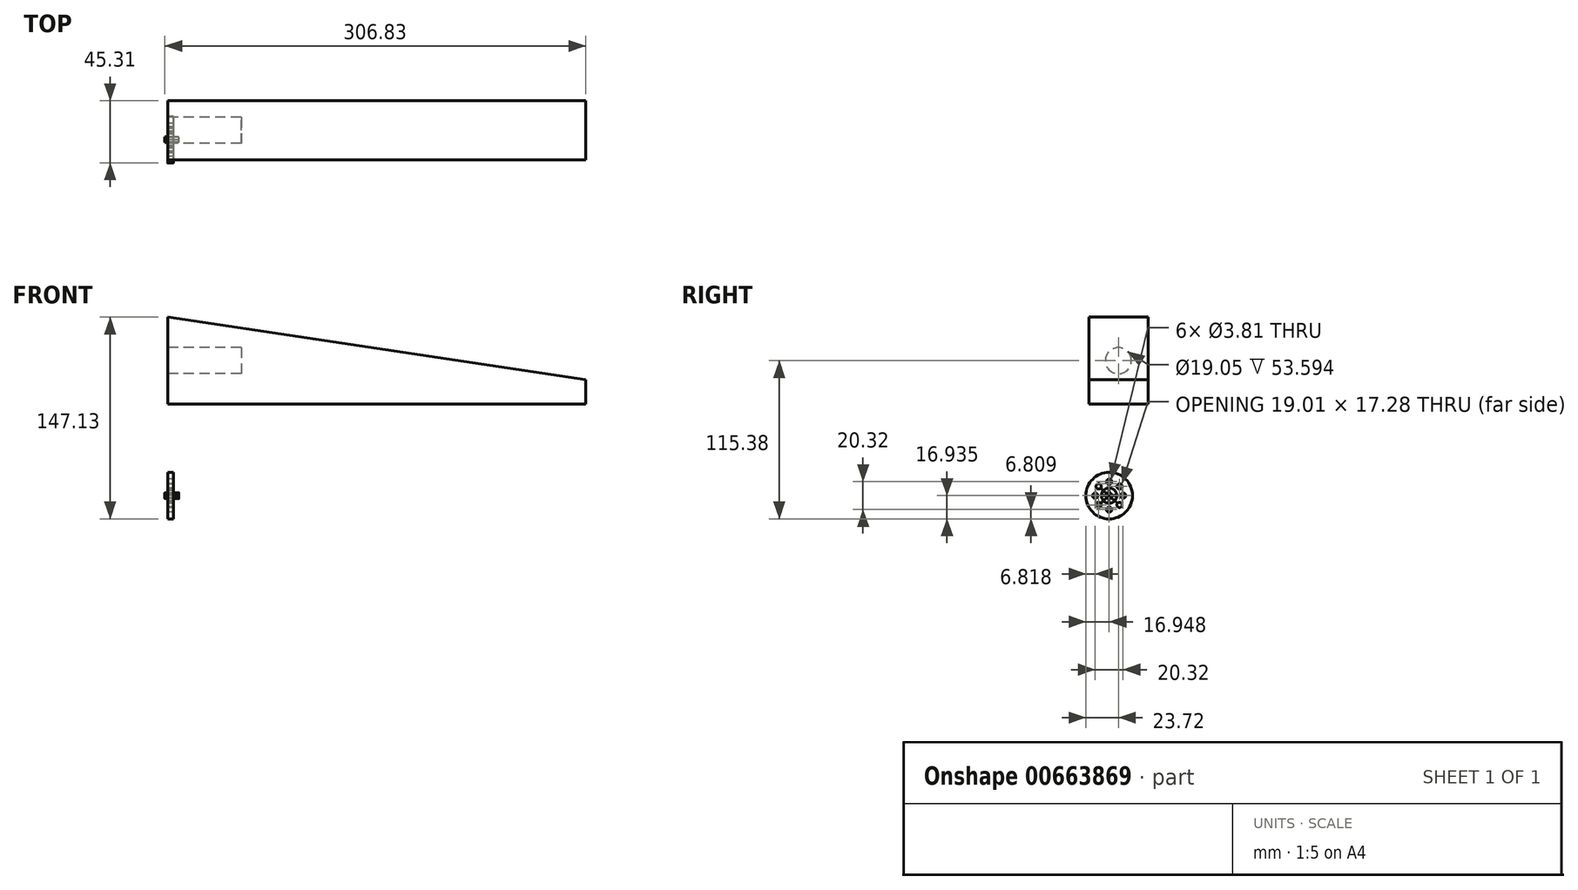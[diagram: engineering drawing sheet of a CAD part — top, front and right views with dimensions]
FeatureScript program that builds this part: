
annotation { "Feature Type Name" : "Feature", "Feature Type Description" : "" }
export const myFeature = defineFeature(function(context is Context, id is Id, definition is map)
    precondition{}
    {
        {
            var Q0;
            Q0=qCreatedBy(makeId("Front.planeOp"),FACE);
            var sketch = newSketch(context, id + "F0", { "sketchPlane" : qUnion([Q0])});
            skLineSegment(sketch, "E0", {"start": v(0, 0) * mm, "end": v(0, 63.5) * mm});
            skLineSegment(sketch, "E1", {"start": v(0, 0) * mm, "end": v(304.8, 0) * mm});
            skLineSegment(sketch, "E2", {"start": v(304.8, 0) * mm, "end": v(304.8, 17.78) * mm});
            skLineSegment(sketch, "E3", {"start": v(304.8, 17.78) * mm, "end": v(0, 63.5) * mm});
            skSolve(sketch);
        }
        {
            var Q0;
            Q0=makeQuery(id+"F0.imprint","IMPRINT",FACE,{"disambiguationData":[TD([[makeQuery(id+"F0.imprint","IMPRINT",EDGE,{"derivedFrom":sQuery(id+"F0.wireOp",EDGE,"E0")}),-1.0]])]});
            extrude(context, id + "F1", {"entities" : qUnion([Q0]), "oppositeDirection" : true, "depth" : 43.18 * mm, "offsetDistance" : 25.4 * mm});
        }
        {
            var Q0;
            Q0=makeQuery(id+"F1.opExtrude","SWEPT_FACE",FACE,{"disambiguationData":[OSD([sQuery(id+"F0.wireOp",EDGE,"E0")])]});
            var sketch = newSketch(context, id + "F2", { "sketchPlane" : qUnion([Q0])});
            skLineSegment(sketch, "E4", {"start": v(0, 0) * mm, "end": v(0, 31.75) * mm});
            skLineSegment(sketch, "E5", {"start": v(0, 31.75) * mm, "end": v(-21.59, 31.75) * mm});
            skCircle(sketch, "E6", {"center": v(-21.59, 31.75) * mm, "radius": 9.53 * mm});
            skSolve(sketch);
        }
        {
            var Q0;
            Q0=makeQuery(id+"F2.imprint","IMPRINT",FACE,{"disambiguationData":[TD([[makeQuery(id+"F2.imprint","IMPRINT",EDGE,{"derivedFrom":sQuery(id+"F2.wireOp",EDGE,"E6")}),1.0]])]});
            extrude(context, id + "F3", {"entities" : qUnion([Q0]), "operationType" : NewBodyOperationType.REMOVE, "oppositeDirection" : true, "depth" : 53.6 * mm, "offsetDistance" : 25.4 * mm});
        }
        {
            var Q0;
            Q0=qCreatedBy(makeId("Right.planeOp"),FACE);
            var sketch = newSketch(context, id + "F4", { "sketchPlane" : qUnion([Q0])});
            skCircle(sketch, "E7", {"center": v(14.85, -66.66) * mm, "radius": 16.97 * mm});
            skCircle(sketch, "E8", {"center": v(14.85, -66.66) * mm, "radius": 5.59 * mm});
            skCircle(sketch, "E9", {"center": v(14.85, -66.66) * mm, "radius": 2.16 * mm});
            skLineSegment(sketch, "E10", {"start": v(14.85, -66.66) * mm, "end": v(14.85, -76.82) * mm});
            skCircle(sketch, "E11", {"center": v(14.85, -76.82) * mm, "radius": 1.9 * mm});
            skLineSegment(sketch, "E12", {"start": v(14.85, -66.66) * mm, "end": v(14.85, -56.5) * mm});
            skCircle(sketch, "E13", {"center": v(14.85, -56.5) * mm, "radius": 1.9 * mm});
            skLineSegment(sketch, "E14", {"start": v(14.85, -66.66) * mm, "end": v(25, -66.66) * mm});
            skCircle(sketch, "E15", {"center": v(25, -66.66) * mm, "radius": 1.9 * mm});
            skLineSegment(sketch, "E16", {"start": v(14.85, -66.66) * mm, "end": v(4.69, -66.66) * mm});
            skCircle(sketch, "E17", {"center": v(4.69, -66.66) * mm, "radius": 1.9 * mm});
            skLineSegment(sketch, "E18", {"start": v(14.85, -66.66) * mm, "end": v(7.22, -59.95) * mm});
            skLineSegment(sketch, "E19", {"start": v(7.22, -59.95) * mm, "end": v(22.42, -73.44) * mm});
            skLineSegment(sketch, "E20", {"start": v(22.42, -73.44) * mm, "end": v(14.85, -66.66) * mm});
            skLineSegment(sketch, "E21", {"start": v(14.85, -66.66) * mm, "end": v(7.22, -73.44) * mm});
            skLineSegment(sketch, "E22", {"start": v(7.22, -73.44) * mm, "end": v(22.42, -59.95) * mm});
            skCircle(sketch, "E23", {"center": v(22.42, -59.95) * mm, "radius": 1.9 * mm});
            skCircle(sketch, "E24", {"center": v(22.42, -73.44) * mm, "radius": 1.9 * mm});
            skCircle(sketch, "E25", {"center": v(7.22, -73.44) * mm, "radius": 1.9 * mm});
            skCircle(sketch, "E26", {"center": v(7.22, -59.95) * mm, "radius": 1.9 * mm});
            skSolve(sketch);
        }
        {
            var Q0;
            {var subQ0=sQuery(id+"F4.wireOp",EDGE,"E10");var subQ1=sQuery(id+"F4.wireOp",EDGE,"E9");var subQ2=makeQuery(id+"F4.imprint","INTERSECT",VERTEX,{"derivedFrom":[subQ1,subQ0]});Q0=makeQuery(id+"F4.imprint","IMPRINT",FACE,{"disambiguationData":[TD([[makeQuery(id+"F4.imprint","IMPRINT",EDGE,{"disambiguationData":[TD([[subQ2,-1.0]])],"derivedFrom":subQ1}),1.0]])]});}
            var Q1;
            {var subQ0=sQuery(id+"F4.wireOp",EDGE,"E22");var subQ1=sQuery(id+"F4.wireOp",EDGE,"E9");var subQ2=makeQuery(id+"F4.imprint","INTERSECT",VERTEX,{"disambiguationData":[OD(1.0)],"derivedFrom":[subQ1,subQ0]});Q1=makeQuery(id+"F4.imprint","IMPRINT",FACE,{"disambiguationData":[TD([[makeQuery(id+"F4.imprint","IMPRINT",EDGE,{"disambiguationData":[TD([[subQ2,-1.0]])],"derivedFrom":subQ1}),1.0]])]});}
            var Q2;
            {var subQ0=sQuery(id+"F4.wireOp",EDGE,"E16");var subQ1=sQuery(id+"F4.wireOp",EDGE,"E9");var subQ2=makeQuery(id+"F4.imprint","INTERSECT",VERTEX,{"derivedFrom":[subQ1,subQ0]});Q2=makeQuery(id+"F4.imprint","IMPRINT",FACE,{"disambiguationData":[TD([[makeQuery(id+"F4.imprint","IMPRINT",EDGE,{"disambiguationData":[TD([[subQ2,-1.0]])],"derivedFrom":subQ1}),1.0]])]});}
            var Q3;
            {var subQ0=sQuery(id+"F4.wireOp",EDGE,"E19");var subQ1=sQuery(id+"F4.wireOp",EDGE,"E9");var subQ2=makeQuery(id+"F4.imprint","INTERSECT",VERTEX,{"disambiguationData":[OD(0.0)],"derivedFrom":[subQ1,subQ0]});Q3=makeQuery(id+"F4.imprint","IMPRINT",FACE,{"disambiguationData":[TD([[makeQuery(id+"F4.imprint","IMPRINT",EDGE,{"disambiguationData":[TD([[subQ2,-1.0]])],"derivedFrom":subQ1}),1.0]])]});}
            var Q4;
            {var subQ0=sQuery(id+"F4.wireOp",EDGE,"E12");var subQ1=sQuery(id+"F4.wireOp",EDGE,"E9");var subQ2=makeQuery(id+"F4.imprint","INTERSECT",VERTEX,{"derivedFrom":[subQ1,subQ0]});Q4=makeQuery(id+"F4.imprint","IMPRINT",FACE,{"disambiguationData":[TD([[makeQuery(id+"F4.imprint","IMPRINT",EDGE,{"disambiguationData":[TD([[subQ2,-1.0]])],"derivedFrom":subQ1}),1.0]])]});}
            var Q5;
            {var subQ0=sQuery(id+"F4.wireOp",EDGE,"E22");var subQ1=sQuery(id+"F4.wireOp",EDGE,"E9");var subQ2=makeQuery(id+"F4.imprint","INTERSECT",VERTEX,{"disambiguationData":[OD(0.0)],"derivedFrom":[subQ1,subQ0]});Q5=makeQuery(id+"F4.imprint","IMPRINT",FACE,{"disambiguationData":[TD([[makeQuery(id+"F4.imprint","IMPRINT",EDGE,{"disambiguationData":[TD([[subQ2,-1.0]])],"derivedFrom":subQ1}),1.0]])]});}
            var Q6;
            {var subQ0=sQuery(id+"F4.wireOp",EDGE,"E22");var subQ1=sQuery(id+"F4.wireOp",EDGE,"E9");var subQ2=makeQuery(id+"F4.imprint","INTERSECT",VERTEX,{"disambiguationData":[OD(0.0)],"derivedFrom":[subQ1,subQ0]});Q6=makeQuery(id+"F4.imprint","IMPRINT",FACE,{"disambiguationData":[TD([[makeQuery(id+"F4.imprint","IMPRINT",EDGE,{"disambiguationData":[TD([[subQ2,1.0]])],"derivedFrom":subQ1}),1.0]])]});}
            var Q7;
            {var subQ0=sQuery(id+"F4.wireOp",EDGE,"E14");var subQ1=sQuery(id+"F4.wireOp",EDGE,"E9");var subQ2=makeQuery(id+"F4.imprint","INTERSECT",VERTEX,{"derivedFrom":[subQ1,subQ0]});Q7=makeQuery(id+"F4.imprint","IMPRINT",FACE,{"disambiguationData":[TD([[makeQuery(id+"F4.imprint","IMPRINT",EDGE,{"disambiguationData":[TD([[subQ2,1.0]])],"derivedFrom":subQ1}),1.0]])]});}
            extrude(context, id + "F5", {"entities" : qUnion([Q0, Q1, Q2, Q3, Q4, Q5, Q6, Q7]), "depth" : 8.13 * mm, "offsetDistance" : 25.4 * mm});
        }
        {
            var Q0;
            Q0 = qSketchRegion(id + "F4", true);
            extrude(context, id + "F6", {"entities" : qUnion([Q0]), "depth" : 4.06 * mm, "offsetDistance" : 25.4 * mm});
        }
        {
            var Q0;
            {var subQ0=sQuery(id+"F4.wireOp",EDGE,"E10");var subQ1=sQuery(id+"F4.wireOp",EDGE,"E8");var subQ2=makeQuery(id+"F4.imprint","INTERSECT",VERTEX,{"derivedFrom":[subQ1,subQ0]});Q0=makeQuery(id+"F4.imprint","IMPRINT",FACE,{"disambiguationData":[TD([[makeQuery(id+"F4.imprint","IMPRINT",EDGE,{"disambiguationData":[TD([[subQ2,1.0]])],"derivedFrom":subQ1}),1.0]])]});}
            extrude(context, id + "F7", {"entities" : qUnion([Q0]), "depth" : 4.06 * mm, "offsetDistance" : 25.4 * mm});
        }
        {
            var Q0;
            {var subQ0=sQuery(id+"F4.wireOp",EDGE,"E10");var subQ1=sQuery(id+"F4.wireOp",EDGE,"E8");var subQ2=makeQuery(id+"F4.imprint","INTERSECT",VERTEX,{"derivedFrom":[subQ1,subQ0]});Q0=makeQuery(id+"F4.imprint","IMPRINT",FACE,{"disambiguationData":[TD([[makeQuery(id+"F4.imprint","IMPRINT",EDGE,{"disambiguationData":[TD([[subQ2,-1.0]])],"derivedFrom":subQ1}),1.0]])]});}
            extrude(context, id + "F8", {"entities" : qUnion([Q0]), "depth" : 4.06 * mm, "offsetDistance" : 25.4 * mm});
        }
        {
            var Q0;
            {var subQ0=sQuery(id+"F4.wireOp",EDGE,"E22");var subQ1=sQuery(id+"F4.wireOp",EDGE,"E8");var subQ2=makeQuery(id+"F4.imprint","INTERSECT",VERTEX,{"disambiguationData":[OD(0.0)],"derivedFrom":[subQ1,subQ0]});Q0=makeQuery(id+"F4.imprint","IMPRINT",FACE,{"disambiguationData":[TD([[makeQuery(id+"F4.imprint","IMPRINT",EDGE,{"disambiguationData":[TD([[subQ2,1.0]])],"derivedFrom":subQ1}),1.0]])]});}
            extrude(context, id + "F9", {"entities" : qUnion([Q0]), "depth" : 4.06 * mm, "offsetDistance" : 25.4 * mm});
        }
        {
            var Q0;
            {var subQ0=sQuery(id+"F4.wireOp",EDGE,"E14");var subQ1=sQuery(id+"F4.wireOp",EDGE,"E8");var subQ2=makeQuery(id+"F4.imprint","INTERSECT",VERTEX,{"derivedFrom":[subQ1,subQ0]});Q0=makeQuery(id+"F4.imprint","IMPRINT",FACE,{"disambiguationData":[TD([[makeQuery(id+"F4.imprint","IMPRINT",EDGE,{"disambiguationData":[TD([[subQ2,1.0]])],"derivedFrom":subQ1}),1.0]])]});}
            extrude(context, id + "F10", {"entities" : qUnion([Q0]), "depth" : 4.06 * mm, "offsetDistance" : 25.4 * mm});
        }
        {
            var Q0;
            {var subQ0=sQuery(id+"F4.wireOp",EDGE,"E12");var subQ1=sQuery(id+"F4.wireOp",EDGE,"E8");var subQ2=makeQuery(id+"F4.imprint","INTERSECT",VERTEX,{"derivedFrom":[subQ1,subQ0]});Q0=makeQuery(id+"F4.imprint","IMPRINT",FACE,{"disambiguationData":[TD([[makeQuery(id+"F4.imprint","IMPRINT",EDGE,{"disambiguationData":[TD([[subQ2,-1.0]])],"derivedFrom":subQ1}),1.0]])]});}
            extrude(context, id + "F11", {"entities" : qUnion([Q0]), "depth" : 4.06 * mm, "offsetDistance" : 25.4 * mm});
        }
        {
            var Q0;
            {var subQ0=sQuery(id+"F4.wireOp",EDGE,"E22");var subQ1=sQuery(id+"F4.wireOp",EDGE,"E8");var subQ2=makeQuery(id+"F4.imprint","INTERSECT",VERTEX,{"disambiguationData":[OD(0.0)],"derivedFrom":[subQ1,subQ0]});Q0=makeQuery(id+"F4.imprint","IMPRINT",FACE,{"disambiguationData":[TD([[makeQuery(id+"F4.imprint","IMPRINT",EDGE,{"disambiguationData":[TD([[subQ2,-1.0]])],"derivedFrom":subQ1}),1.0]])]});}
            extrude(context, id + "F12", {"entities" : qUnion([Q0]), "depth" : 4.06 * mm, "offsetDistance" : 25.4 * mm});
        }
        {
            var Q0;
            {var subQ0=sQuery(id+"F4.wireOp",EDGE,"E16");var subQ1=sQuery(id+"F4.wireOp",EDGE,"E8");var subQ2=makeQuery(id+"F4.imprint","INTERSECT",VERTEX,{"derivedFrom":[subQ1,subQ0]});Q0=makeQuery(id+"F4.imprint","IMPRINT",FACE,{"disambiguationData":[TD([[makeQuery(id+"F4.imprint","IMPRINT",EDGE,{"disambiguationData":[TD([[subQ2,1.0]])],"derivedFrom":subQ1}),1.0]])]});}
            extrude(context, id + "F13", {"entities" : qUnion([Q0]), "depth" : 4.06 * mm, "offsetDistance" : 25.4 * mm});
        }
        {
            var Q0;
            {var subQ0=sQuery(id+"F4.wireOp",EDGE,"E16");var subQ1=sQuery(id+"F4.wireOp",EDGE,"E8");var subQ2=makeQuery(id+"F4.imprint","INTERSECT",VERTEX,{"derivedFrom":[subQ1,subQ0]});Q0=makeQuery(id+"F4.imprint","IMPRINT",FACE,{"disambiguationData":[TD([[makeQuery(id+"F4.imprint","IMPRINT",EDGE,{"disambiguationData":[TD([[subQ2,-1.0]])],"derivedFrom":subQ1}),1.0]])]});}
            extrude(context, id + "F14", {"entities" : qUnion([Q0]), "depth" : 4.06 * mm, "offsetDistance" : 25.4 * mm});
        }
        {
            var Q0;
            Q0=makeQuery(id+"F5.opExtrude","CAP_FACE",FACE,{"disambiguationData":[OSD([sQuery(id+"F4.wireOp",EDGE,"E9"),sQuery(id+"F4.wireOp",EDGE,"E14"),sQuery(id+"F4.wireOp",EDGE,"E18"),sQuery(id+"F4.wireOp",EDGE,"E20"),sQuery(id+"F4.wireOp",EDGE,"E22")])],"isStart":true});
            var Q1;
            Q1=makeQuery(id+"F5.opExtrude","CAP_FACE",FACE,{"disambiguationData":[OSD([sQuery(id+"F4.wireOp",EDGE,"E9"),sQuery(id+"F4.wireOp",EDGE,"E19"),sQuery(id+"F4.wireOp",EDGE,"E22")])],"isStart":true});
            var Q2;
            Q2=makeQuery(id+"F5.opExtrude","CAP_FACE",FACE,{"disambiguationData":[OSD([sQuery(id+"F4.wireOp",EDGE,"E9"),sQuery(id+"F4.wireOp",EDGE,"E19"),sQuery(id+"F4.wireOp",EDGE,"E21")])],"isStart":true});
            extrude(context, id + "F15", {"entities" : qUnion([Q0, Q1, Q2]), "depth" : 2.03 * mm, "offsetDistance" : 25.4 * mm});
        }
    });
